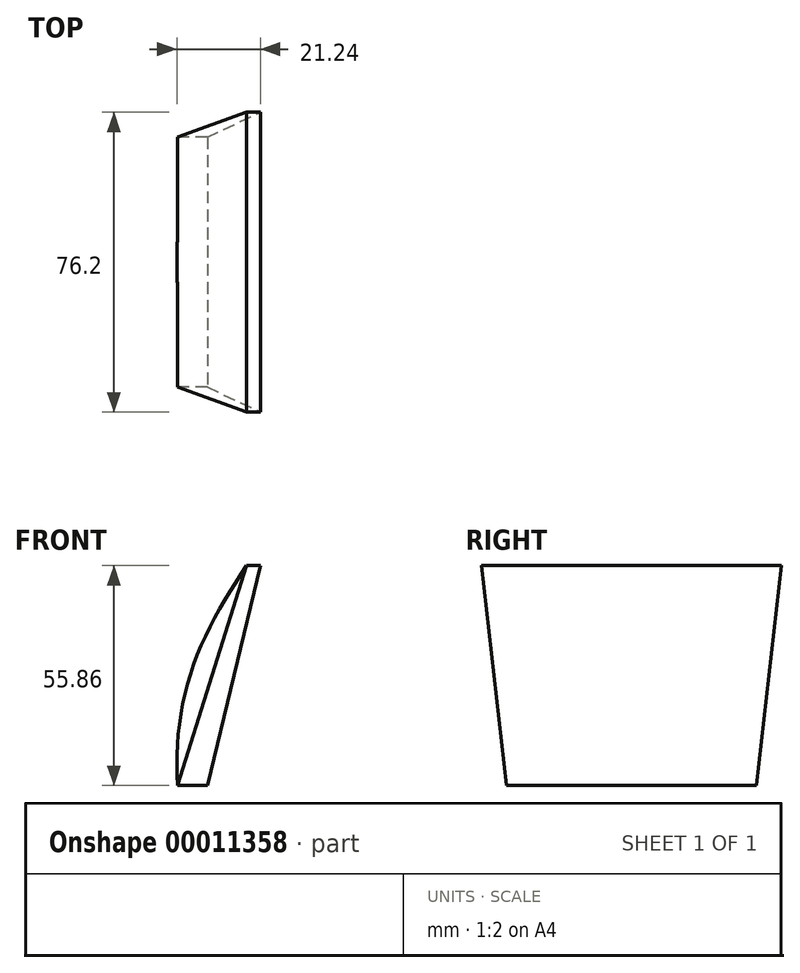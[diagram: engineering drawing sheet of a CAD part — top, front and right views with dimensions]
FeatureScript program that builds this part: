
annotation { "Feature Type Name" : "Feature", "Feature Type Description" : "" }
export const myFeature = defineFeature(function(context is Context, id is Id, definition is map)
    precondition{}
    {
        {
            var Q0;
            Q0=qCreatedBy(makeId("Front.planeOp"),FACE);
            var sketch = newSketch(context, id + "F0", { "sketchPlane" : qUnion([Q0])});
            skFitSpline(sketch, "E0", {"points": [v(0, 0) * mm, v(0, 10.3) * mm, v(2.2, 24.3) * mm, v(8.23, 40.21) * mm, v(17.57, 55.86) * mm], "startDerivative": vector(-1.53, 47.54) * mm, "endDerivative": vector(35.79, 55.52) * mm});
            skSolve(sketch);
        }
        {
            var Q0;
            Q0=qCreatedBy(makeId("Top.planeOp"),FACE);
            var sketch = newSketch(context, id + "F1", { "sketchPlane" : qUnion([Q0])});
            skLineSegment(sketch, "E1.rect.bottom", {"start": v(7.62, 31.75) * mm, "end": v(0, 31.75) * mm});
            skLineSegment(sketch, "E1.rect.top", {"start": v(7.62, -31.75) * mm, "end": v(0, -31.75) * mm});
            skLineSegment(sketch, "E1.rect.left", {"start": v(7.62, 31.75) * mm, "end": v(7.62, -31.75) * mm});
            skLineSegment(sketch, "E1.rect.right", {"start": v(0, 31.75) * mm, "end": v(0, -31.75) * mm});
            skPoint(sketch, "E1.rect.middle", {"position": v(3.81, 0) * mm});
            skSolve(sketch);
        }
        {
            var Q0;
            Q0=sQuery(id+"F0.wireOp",VERTEX,"E0.end");
            var Q1;
            Q1=qCreatedBy(makeId("Top.planeOp"),FACE);
            cPlane(context, id + "F2", {"entities" : qUnion([Q0, Q1]), "cplaneType" : CPlaneType.PLANE_POINT, "offset" : 152.4 * mm, "width" : 152.4 * mm, "height" : 152.4 * mm});
        }
        {
            var Q0;
            Q0=qCreatedBy(id+"F2.planeOp",FACE);
            var sketch = newSketch(context, id + "F3", { "sketchPlane" : qUnion([Q0])});
            skLineSegment(sketch, "E2.rect.bottom", {"start": v(17.57, -38.1) * mm, "end": v(21.12, -38.1) * mm});
            skLineSegment(sketch, "E2.rect.top", {"start": v(17.57, 38.1) * mm, "end": v(21.12, 38.1) * mm});
            skLineSegment(sketch, "E2.rect.left", {"start": v(17.57, -38.1) * mm, "end": v(17.57, 38.1) * mm});
            skLineSegment(sketch, "E2.rect.right", {"start": v(21.12, -38.1) * mm, "end": v(21.12, 38.1) * mm});
            skSolve(sketch);
        }
        {
            var Q0;
            Q0=makeQuery(id+"F1.imprint","IMPRINT",FACE,{"disambiguationData":[TD([[makeQuery(id+"F1.imprint","IMPRINT",EDGE,{"derivedFrom":sQuery(id+"F1.wireOp",EDGE,"E1.rect.bottom")}),1.0]])]});
            var Q1;
            Q1=makeQuery(id+"F3.imprint","IMPRINT",FACE,{"disambiguationData":[TD([[makeQuery(id+"F3.imprint","IMPRINT",EDGE,{"derivedFrom":sQuery(id+"F3.wireOp",EDGE,"E2.rect.bottom")}),1.0]])]});
            var Q2;
            Q2=sQuery(id+"F0.wireOp",EDGE,"E0");
            loft(context, id + "F4", {"addGuides" : true, "sheetProfilesArray" : [{ "sheetProfileEntities" : qUnion([Q0]) }, { "sheetProfileEntities" : qUnion([Q1]) }], "guidesArray" : [{ "guideEntities" : qUnion([Q2]), "guideDerivativeType" : LoftGuideDerivativeType.DEFAULT, "guideDerivativeMagnitude" : 1 }]});
        }
    });
